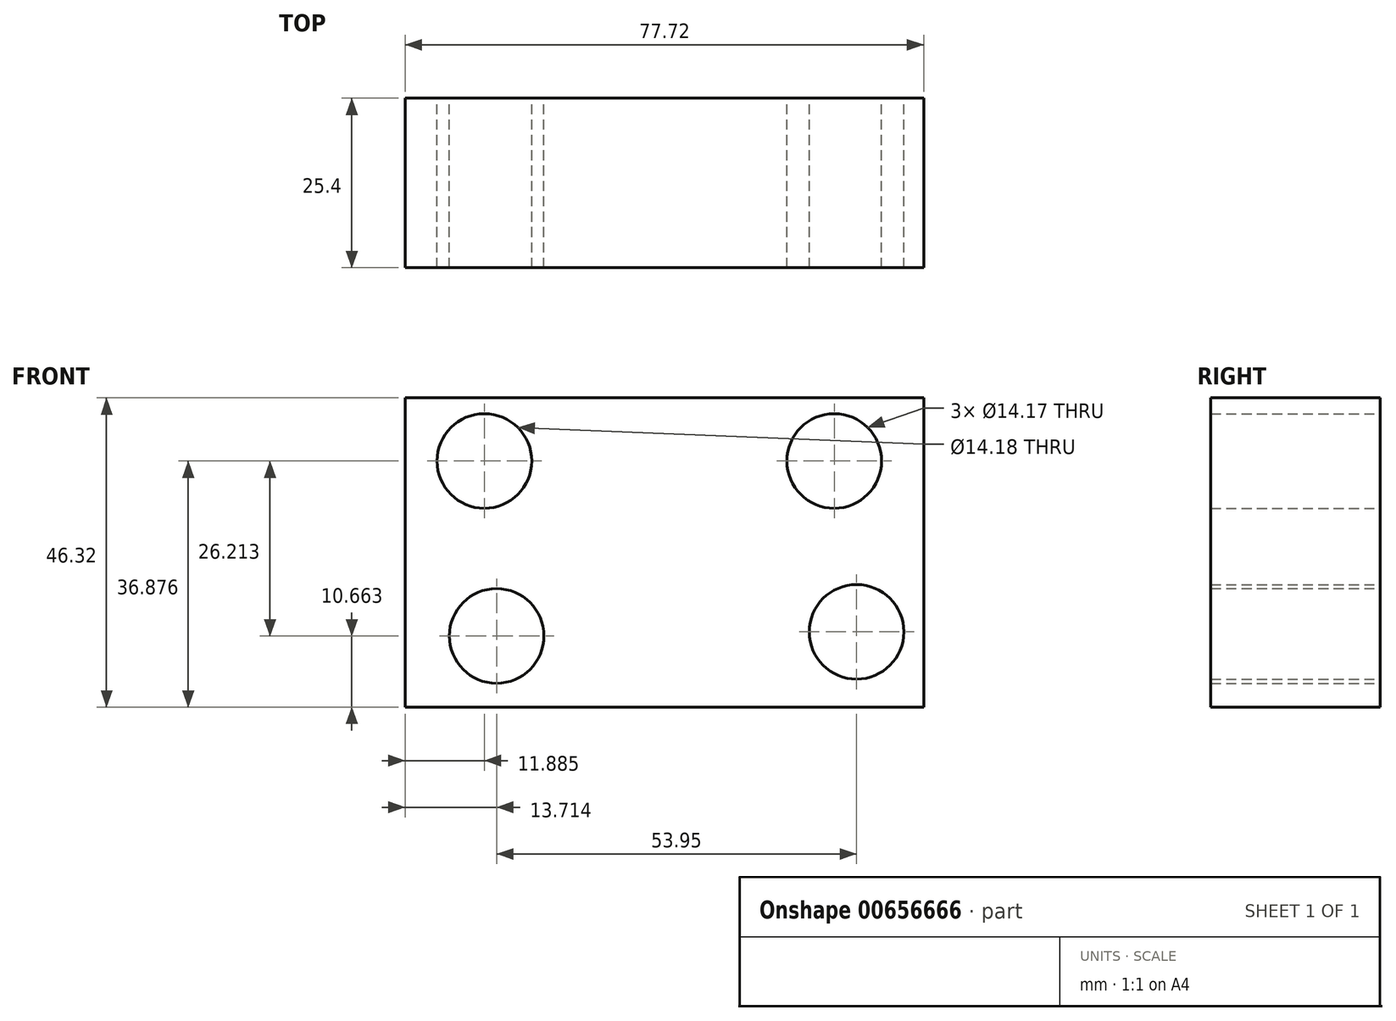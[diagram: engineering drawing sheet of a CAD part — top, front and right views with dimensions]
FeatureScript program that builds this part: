
annotation { "Feature Type Name" : "Feature", "Feature Type Description" : "" }
export const myFeature = defineFeature(function(context is Context, id is Id, definition is map)
    precondition{}
    {
        {
            var Q0;
            Q0=qCreatedBy(makeId("Front.planeOp"),FACE);
            var sketch = newSketch(context, id + "F0", { "sketchPlane" : qUnion([Q0])});
            skLineSegment(sketch, "E0.bottom", {"start": v(-38.86, 23.16) * mm, "end": v(38.86, 23.16) * mm});
            skLineSegment(sketch, "E0.top", {"start": v(-38.86, -23.16) * mm, "end": v(38.86, -23.16) * mm});
            skLineSegment(sketch, "E0.left", {"start": v(-38.86, 23.16) * mm, "end": v(-38.86, -23.16) * mm});
            skLineSegment(sketch, "E0.right", {"start": v(38.86, 23.16) * mm, "end": v(38.86, -23.16) * mm});
            skPoint(sketch, "E0.middle", {"position": v(0, 0) * mm});
            skCircle(sketch, "E1", {"center": v(-26.97, 13.72) * mm, "radius": 7.09 * mm});
            skCircle(sketch, "E2", {"center": v(25.45, 13.72) * mm, "radius": 7.09 * mm});
            skCircle(sketch, "E3", {"center": v(28.8, -11.89) * mm, "radius": 7.09 * mm});
            skCircle(sketch, "E4", {"center": v(-25.15, -12.5) * mm, "radius": 7.09 * mm});
            skSolve(sketch);
        }
        {
            var Q0;
            Q0 = qSketchRegion(id + "F0", true);
            extrude(context, id + "F1", {"entities" : qUnion([Q0]), "depth" : 25.4 * mm, "offsetDistance" : 25.4 * mm});
        }
    });
